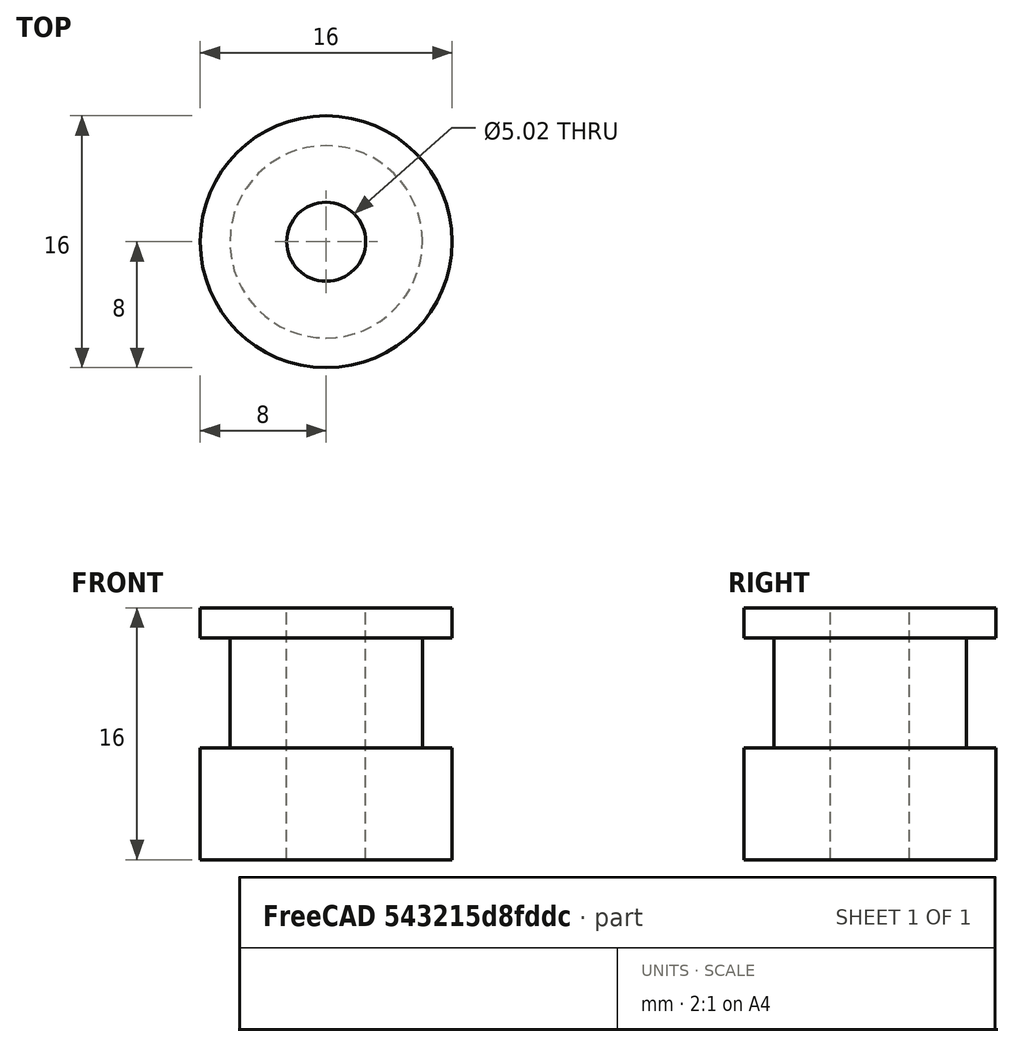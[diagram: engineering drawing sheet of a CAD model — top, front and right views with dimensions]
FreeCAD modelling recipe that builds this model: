
FCSTD DOCUMENT  (FreeCAD 0.20R29410 (Git))
Label: TimingPulleyGT2
License: All rights reserved
LicenseURL: http://en.wikipedia.org/wiki/All_rights_reserved
objects: App::DocumentObjectGroup×3, PartDesign::CoordinateSystem×1, App::FeaturePython×1, Sketcher::SketchObject×1, PartDesign::Revolution×1, PartDesign::Body×1, App::Part×1
note: 5 computed .brp shape members not serialized (recipe doc carries the construction recipe); baked Part::Feature solids carry a one-line shape summary decoded from their .brp

FEATURE [App::DocumentObjectGroup] Parts
FEATURE [PartDesign::CoordinateSystem] LCS_Origin
  AttacherType = Attacher::AttachEngine3D
  MapMode = 2
  Support = -> [X_Axis]
FEATURE [App::FeaturePython] Variables  # WARN: FeaturePython — macro-defined, semantics opaque (R4)
  Type = App::PropertyContainer
FEATURE [App::DocumentObjectGroup] Constraints
FEATURE [App::DocumentObjectGroup] Configurations
FEATURE [Sketcher::SketchObject] Sketch
  FullyConstrained = true
  MapMode = 5
  Placement = pos=(0,0,0) rot=(1,0,0;1.5708rad)
  Support = -> [XZ_Plane001]
  sketch-geometry (8):
    g0: LineSegment StartX=2.51 StartY=0 StartZ=0 EndX=2.51 EndY=16 EndZ=0
    g1: LineSegment StartX=2.51 StartY=16 StartZ=0 EndX=8 EndY=16 EndZ=0
    g2: LineSegment StartX=8 StartY=16 StartZ=0 EndX=8 EndY=14.1 EndZ=0
    g3: LineSegment StartX=8 StartY=14.1 StartZ=0 EndX=6.11 EndY=14.1 EndZ=0
    g4: LineSegment StartX=6.11 StartY=14.1 StartZ=0 EndX=6.11 EndY=7.1 EndZ=0
    g5: LineSegment StartX=6.11 StartY=7.1 StartZ=0 EndX=8 EndY=7.1 EndZ=0
    g6: LineSegment StartX=8 StartY=7.1 StartZ=0 EndX=8 EndY=0 EndZ=0
    g7: LineSegment StartX=8 StartY=0 StartZ=0 EndX=2.51 EndY=0 EndZ=0
  constraints (24):
    c: PointOnObject(g0,g-1)
    c: Vertical(g0)
    c: Coincident(g0,g1)
    c: Horizontal(g1)
    c: Coincident(g1,g2)
    c: Coincident(g2,g3)
    c: Horizontal(g3)
    c: Coincident(g3,g4)
    c: Vertical(g4)
    c: Coincident(g4,g5)
    c: Horizontal(g5)
    c: Coincident(g5,g6)
    c: PointOnObject(g6,g-1)
    c: Vertical(g6)
    c: Coincident(g6,g7)
    c: Coincident(g7,g0)
    c: Vertical(g2)
    c: DistanceX(g-1,g3) = 6.11
    c: DistanceX(g-1,g0) = 2.51
    c: DistanceY(g4,g4) = 7
    c: PointOnObject(g2,g6)
    c: DistanceY(g6,g6) = 7.1
    c: DistanceX(g-1,g6) = 8
    c: DistanceY(g-1,g0) = 16
FEATURE [PartDesign::Revolution] Revolution
  Angle = 360
  Axis = (0,2e-16,1)
  Base = (0,0,0)
  Placement = pos=(0,0,0) rot=(1,0,0;1.5708rad)
  Profile = -> Sketch
  ReferenceAxis = -> Sketch [V_Axis]
  Reversed = true
FEATURE [PartDesign::Body] Body
  Group = -> [Sketch,Revolution]
  Origin = -> Origin001
  Tip = -> Revolution
FEATURE [App::Part] Assembly
  AssemblyType = Part::Link
  Group = -> [LCS_Origin,Variables,Constraints,Configurations,Body]
  Origin = -> Origin
  Type = Assembly
